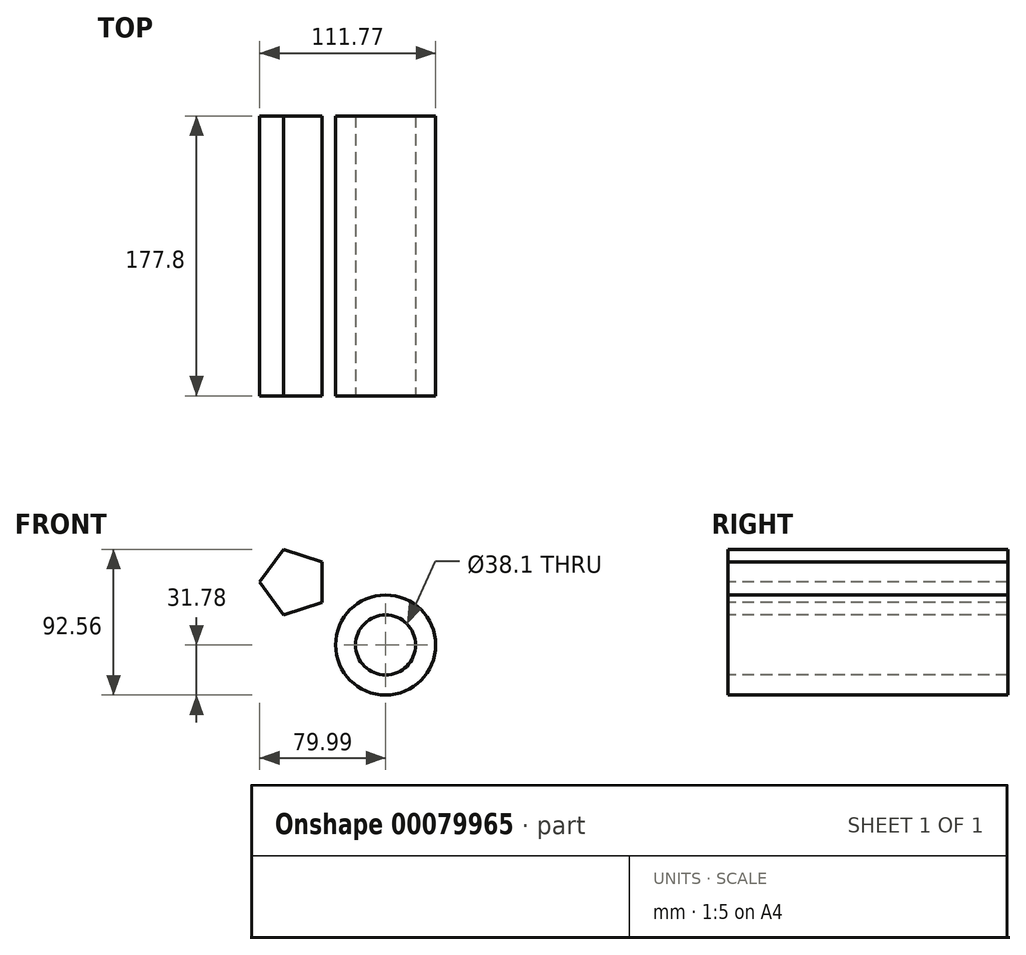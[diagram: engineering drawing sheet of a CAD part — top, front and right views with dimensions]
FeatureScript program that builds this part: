
annotation { "Feature Type Name" : "Feature", "Feature Type Description" : "" }
export const myFeature = defineFeature(function(context is Context, id is Id, definition is map)
    precondition{}
    {
        {
            var Q0;
            Q0=qCreatedBy(makeId("Front.planeOp"),FACE);
            var sketch = newSketch(context, id + "F0", { "sketchPlane" : qUnion([Q0])});
            skCircle(sketch, "E0", {"center": v(0, 0) * mm, "radius": 31.78 * mm});
            skSolve(sketch);
        }
        {
            var Q0;
            Q0=makeQuery(id+"F0.imprint","IMPRINT",FACE,{"disambiguationData":[TD([[makeQuery(id+"F0.imprint","IMPRINT",EDGE,{"derivedFrom":sQuery(id+"F0.wireOp",EDGE,"E0")}),1.0]])]});
            extrude(context, id + "F1", {"entities" : qUnion([Q0]), "oppositeDirection" : true, "depth" : 177.8 * mm});
        }
        {
            var Q0;
            Q0=makeQuery(id+"F1.opExtrude","CAP_FACE",FACE,{"disambiguationData":[OSD([sQuery(id+"F0.wireOp",EDGE,"E0")])],"isStart":true});
            var sketch = newSketch(context, id + "F2", { "sketchPlane" : qUnion([Q0])});
            skCircle(sketch, "E1", {"center": v(0, 0) * mm, "radius": 19.1 * mm});
            skSolve(sketch);
        }
        {
            var Q0;
            Q0=sQuery(id+"F2.wireOp",VERTEX,"E1.center");
            var Q1;
            Q1=makeQuery(id+"F1.opExtrude","SWEPT_BODY",BODY,{"disambiguationData":[OSD([sQuery(id+"F0.wireOp",EDGE,"E0")])]});
            hole(context, id + "F3", {"style" : HoleStyle.SIMPLE, "endStyle" : HoleEndStyle.THROUGH, "holeDiameter" : 38.1 * mm, "locations" : qUnion([Q0]), "scope" : qUnion([Q1]), "isTappedThrough" : true});
        }
        {
            var Q0;
            Q0=qCreatedBy(makeId("Front.planeOp"),FACE);
            var sketch = newSketch(context, id + "F4", { "sketchPlane" : qUnion([Q0])});
            skCircle(sketch, "E2.cCircle", {"center": v(-58.14, 40) * mm, "radius": 17.67 * mm, "construction": true});
            skLineSegment(sketch, "E2.0", {"start": v(-40.47, 52.84) * mm, "end": v(-40.47, 27.17) * mm});
            skLineSegment(sketch, "E2.1", {"start": v(-40.47, 27.17) * mm, "end": v(-64.9, 19.23) * mm});
            skLineSegment(sketch, "E2.2", {"start": v(-64.9, 19.23) * mm, "end": v(-79.99, 40) * mm});
            skLineSegment(sketch, "E2.3", {"start": v(-79.99, 40) * mm, "end": v(-64.9, 60.78) * mm});
            skLineSegment(sketch, "E2.4", {"start": v(-64.9, 60.78) * mm, "end": v(-40.47, 52.84) * mm});
            skPoint(sketch, "E2.0.midPoint", {"position": v(-40.47, 40) * mm});
            skSolve(sketch);
        }
        {
            var Q0;
            Q0=makeQuery(id+"F4.imprint","IMPRINT",FACE,{"disambiguationData":[TD([[makeQuery(id+"F4.imprint","IMPRINT",EDGE,{"derivedFrom":sQuery(id+"F4.wireOp",EDGE,"E2.0")}),-1.0]])]});
            var Q1;
            Q1 = qSketchRegion(id + "F4", true);
            extrude(context, id + "F5", {"entities" : qUnion([Q0, Q1]), "oppositeDirection" : true, "depth" : 177.8 * mm});
        }
    });
